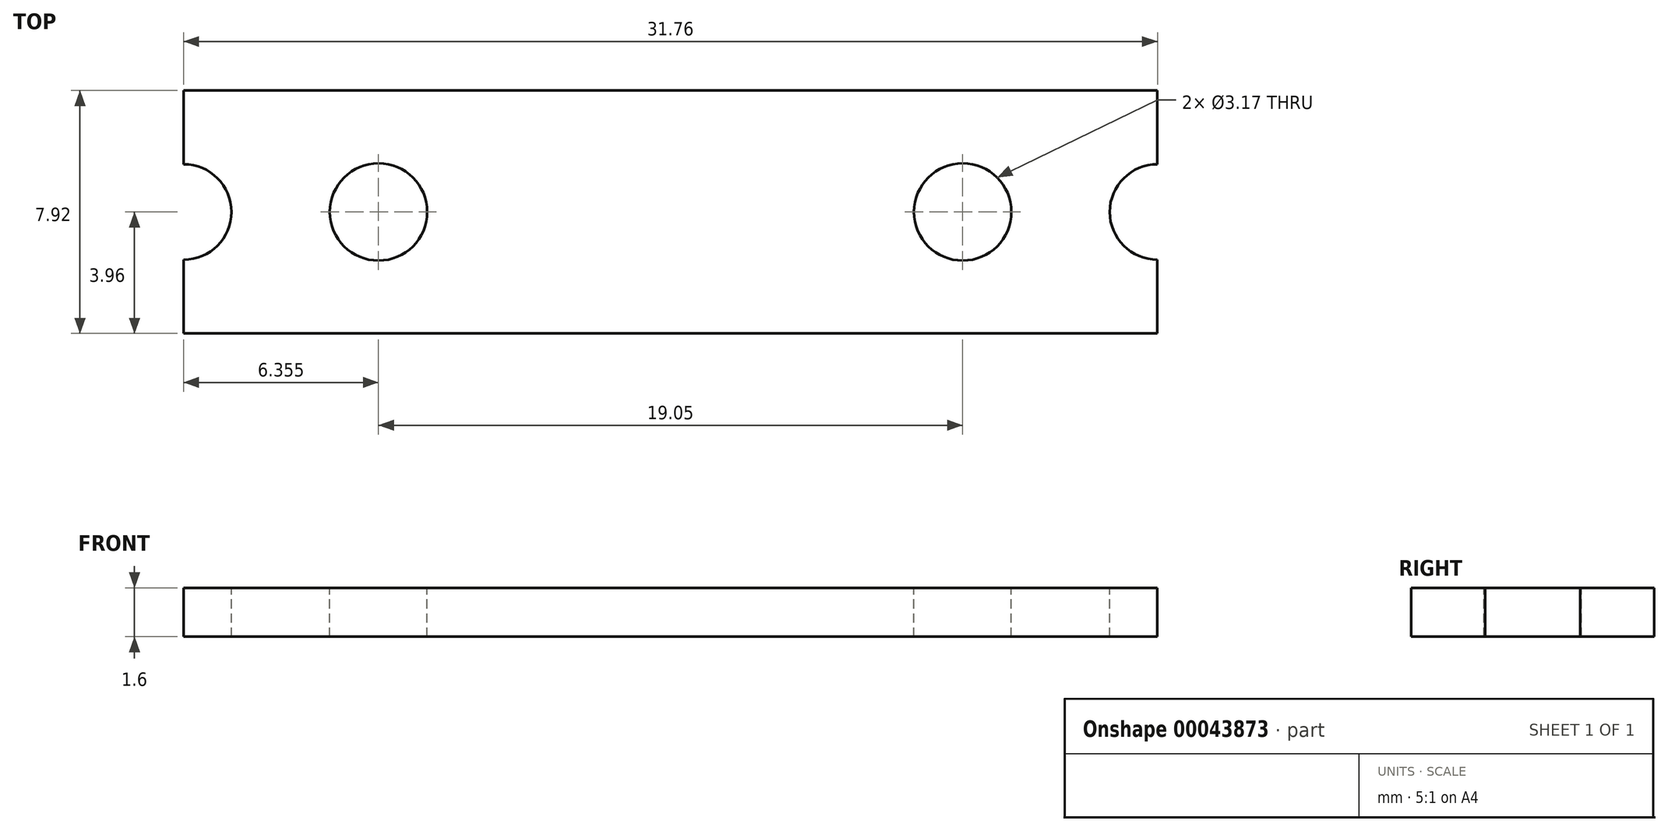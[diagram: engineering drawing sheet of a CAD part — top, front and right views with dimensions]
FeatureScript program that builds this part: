
annotation { "Feature Type Name" : "Feature", "Feature Type Description" : "" }
export const myFeature = defineFeature(function(context is Context, id is Id, definition is map)
    precondition{}
    {
        {
            var Q0;
            Q0=qCreatedBy(makeId("Front.planeOp"),FACE);
            var sketch = newSketch(context, id + "F0", { "sketchPlane" : qUnion([Q0])});
            skLineSegment(sketch, "E0.rect.bottom", {"start": v(15.88, -0.8) * mm, "end": v(-15.88, -0.8) * mm});
            skLineSegment(sketch, "E0.rect.top", {"start": v(15.88, 0.8) * mm, "end": v(-15.88, 0.8) * mm});
            skLineSegment(sketch, "E0.rect.left", {"start": v(15.88, -0.8) * mm, "end": v(15.88, 0.8) * mm});
            skLineSegment(sketch, "E0.rect.right", {"start": v(-15.88, -0.8) * mm, "end": v(-15.88, 0.8) * mm});
            skPoint(sketch, "E0.rect.middle", {"position": v(0, 0) * mm});
            skSolve(sketch);
        }
        {
            var Q0;
            Q0 = qSketchRegion(id + "F0", true);
            extrude(context, id + "F1", {"entities" : qUnion([Q0]), "endBound" : BoundingType.SYMMETRIC, "depth" : 7.92 * mm});
        }
        {
            var Q0;
            Q0=makeQuery(id+"F1.opExtrude","SWEPT_FACE",FACE,{"disambiguationData":[OSD([sQuery(id+"F0.wireOp",EDGE,"E0.rect.top")])]});
            var sketch = newSketch(context, id + "F2", { "sketchPlane" : qUnion([Q0])});
            skCircle(sketch, "E1", {"center": v(-9.53, 0) * mm, "radius": 1.59 * mm});
            skCircle(sketch, "E2.MirrorC", {"center": v(9.53, 0) * mm, "radius": 1.59 * mm});
            skCircle(sketch, "E3", {"center": v(-15.88, 0) * mm, "radius": 1.55 * mm});
            skCircle(sketch, "E4.MirrorC", {"center": v(15.88, 0) * mm, "radius": 1.55 * mm});
            skSolve(sketch);
        }
        {
            var Q0;
            Q0 = qSketchRegion(id + "F2", true);
            extrude(context, id + "F3", {"entities" : qUnion([Q0]), "operationType" : NewBodyOperationType.REMOVE, "endBound" : BoundingType.THROUGH_ALL, "oppositeDirection" : true, "depth" : 25 * mm});
        }
    });
